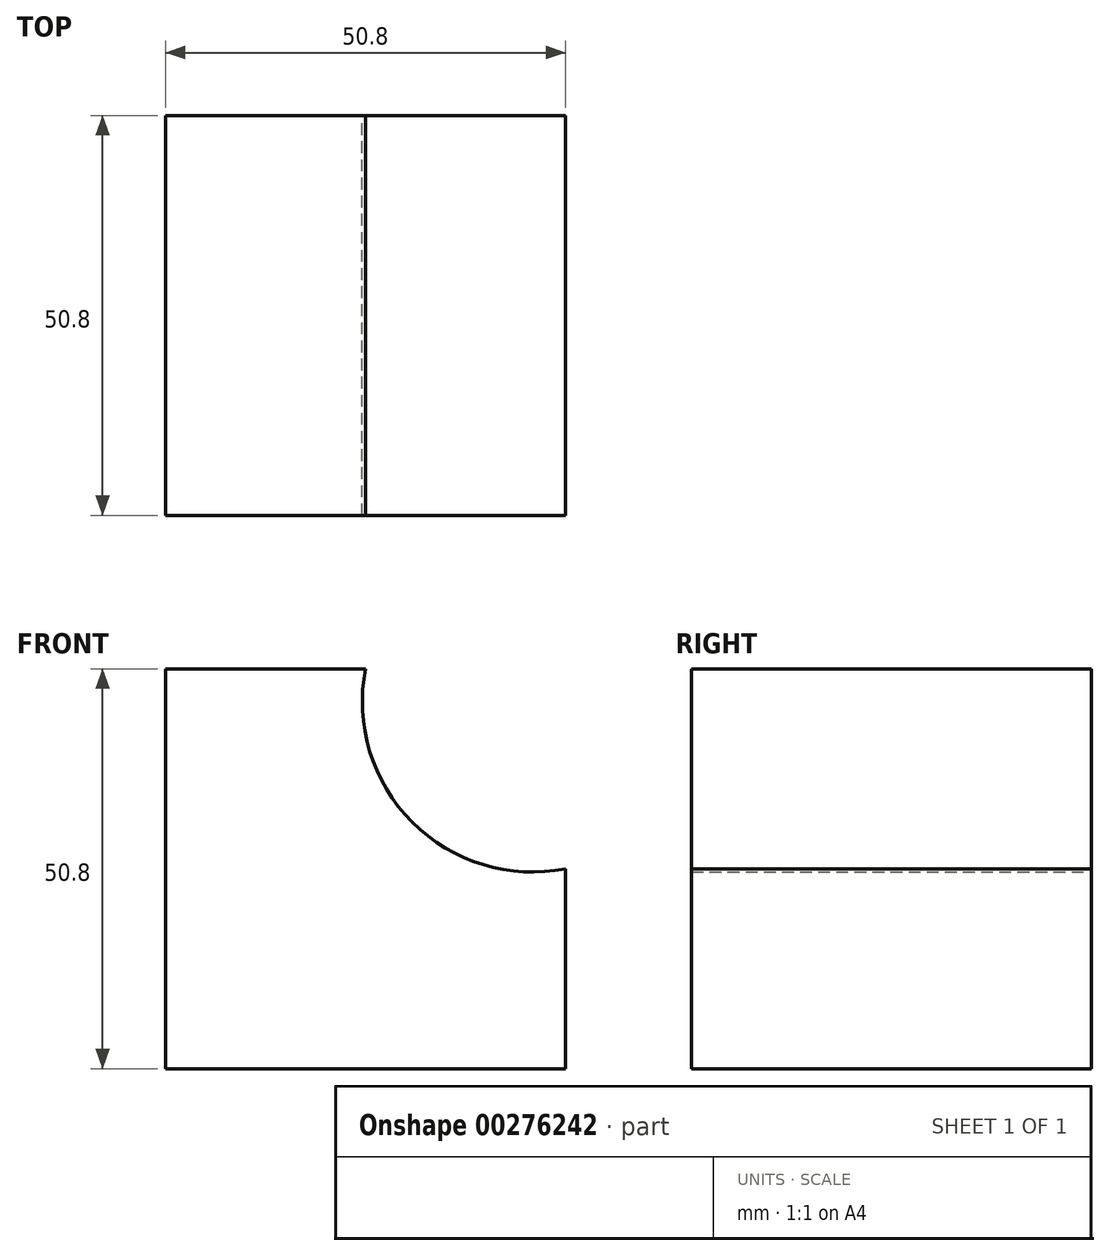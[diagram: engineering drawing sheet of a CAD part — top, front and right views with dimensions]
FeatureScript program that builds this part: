
annotation { "Feature Type Name" : "Feature", "Feature Type Description" : "" }
export const myFeature = defineFeature(function(context is Context, id is Id, definition is map)
    precondition{}
    {
        {
            var Q0;
            Q0=qCreatedBy(makeId("Front.planeOp"),FACE);
            var sketch = newSketch(context, id + "F0", { "sketchPlane" : qUnion([Q0])});
            skLineSegment(sketch, "E0", {"start": v(-69.97, 61.24) * mm, "end": v(-69.97, 10.44) * mm});
            skLineSegment(sketch, "E1", {"start": v(-69.97, 10.44) * mm, "end": v(-19.17, 10.44) * mm});
            skLineSegment(sketch, "E2", {"start": v(-19.17, 10.44) * mm, "end": v(-19.17, 35.84) * mm});
            skLineSegment(sketch, "E3", {"start": v(-69.97, 61.24) * mm, "end": v(-44.57, 61.24) * mm});
            skArc(sketch, "E4", {"start": v(-44.57, 61.24) * mm, "mid": v(-38.65, 41.76) * mm, "end": v(-19.17, 35.84) * mm});
            skSolve(sketch);
        }
        {
            var Q0;
            Q0 = qSketchRegion(id + "F0", true);
            extrude(context, id + "F1", {"entities" : qUnion([Q0]), "depth" : 50.8 * mm});
        }
    });
